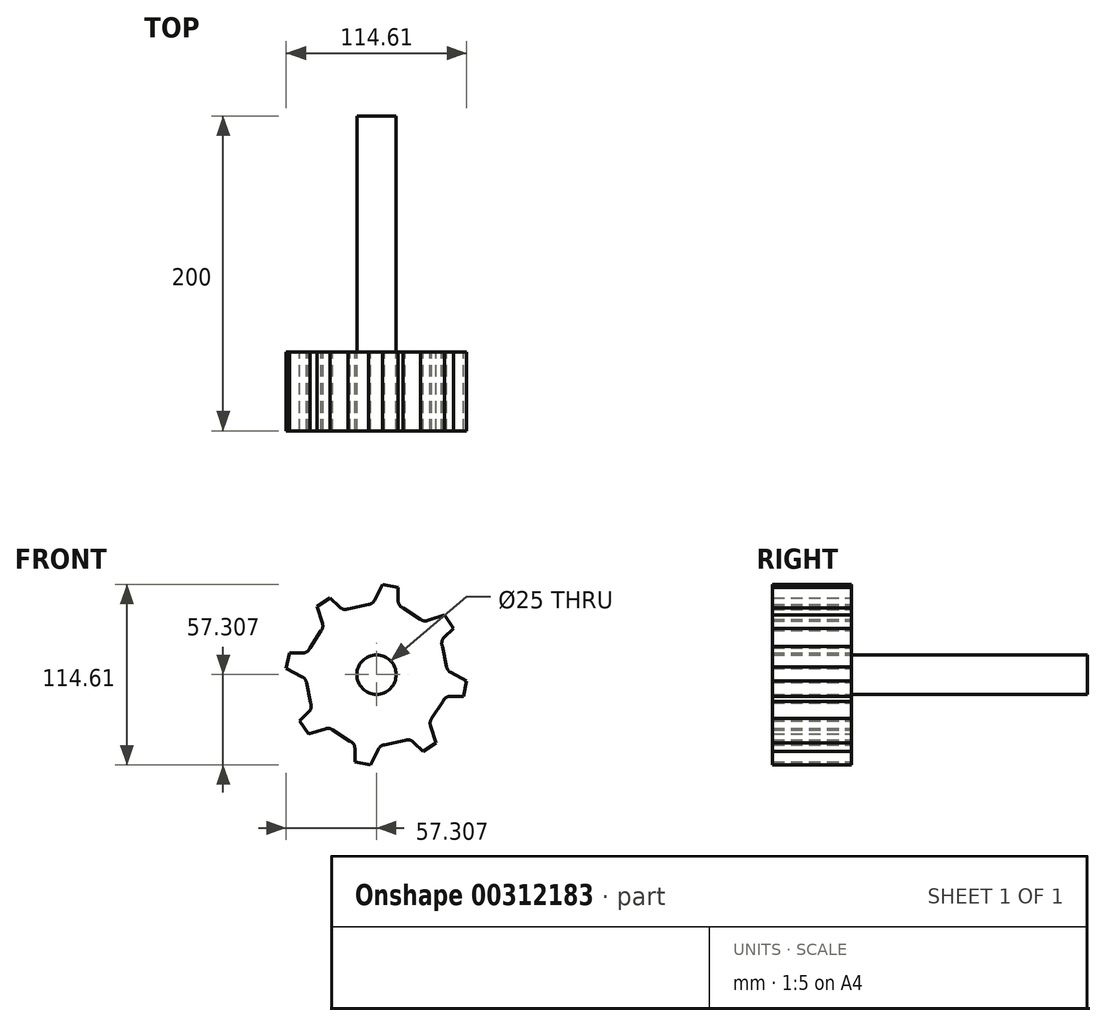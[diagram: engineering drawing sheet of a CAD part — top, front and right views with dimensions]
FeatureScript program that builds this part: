
annotation { "Feature Type Name" : "Feature", "Feature Type Description" : "" }
export const myFeature = defineFeature(function(context is Context, id is Id, definition is map)
    precondition{}
    {
        {
            var Q0;
            Q0=qCreatedBy(makeId("Front.planeOp"),FACE);
            var sketch = newSketch(context, id + "F0", { "sketchPlane" : qUnion([Q0])});
            skLineSegment(sketch, "E0.bottom", {"start": v(250, -250) * mm, "end": v(-250, -250) * mm});
            skLineSegment(sketch, "E0.top", {"start": v(250, 250) * mm, "end": v(-250, 250) * mm});
            skLineSegment(sketch, "E0.left", {"start": v(250, -250) * mm, "end": v(250, 250) * mm});
            skLineSegment(sketch, "E0.right", {"start": v(-250, -250) * mm, "end": v(-250, 250) * mm});
            skLineSegment(sketch, "E1", {"start": v(-125.88, -126.38) * mm, "end": v(-116.04, -128.34) * mm});
            skLineSegment(sketch, "E2", {"start": v(-116.04, -128.34) * mm, "end": v(-116.04, -136.75) * mm});
            skLineSegment(sketch, "E3", {"start": v(-125.88, -126.38) * mm, "end": v(-131.1, -136.48) * mm});
            skPoint(sketch, "E4.visualSharp", {"position": v(-116.04, -140.12) * mm});
            skArc(sketch, "E4.filletArc", {"start": v(-116.04, -136.75) * mm, "mid": v(-115.18, -139.55) * mm, "end": v(-112.9, -141.39) * mm});
            skPoint(sketch, "E5.visualSharp", {"position": v(-132.28, -138.75) * mm});
            skArc(sketch, "E5.filletArc", {"start": v(-134.8, -139.13) * mm, "mid": v(-132.63, -138.25) * mm, "end": v(-131.1, -136.48) * mm});
            skLineSegment(sketch, "E6.1.0", {"start": v(-159.2, -134.84) * mm, "end": v(-153.25, -140.78) * mm});
            skArc(sketch, "E6.1.1", {"start": v(-153.25, -140.78) * mm, "mid": v(-150.66, -142.16) * mm, "end": v(-147.76, -141.85) * mm});
            skLineSegment(sketch, "E6.1.3", {"start": v(-167.54, -140.4) * mm, "end": v(-159.2, -134.84) * mm});
            skLineSegment(sketch, "E6.1.4", {"start": v(-167.54, -140.4) * mm, "end": v(-164.09, -151.25) * mm});
            skArc(sketch, "E6.1.5", {"start": v(-164.83, -155.74) * mm, "mid": v(-163.92, -153.58) * mm, "end": v(-164.09, -151.25) * mm});
            skLineSegment(sketch, "E6.1.6", {"start": v(-164.83, -155.74) * mm, "end": v(-166.01, -157.33) * mm});
            skLineSegment(sketch, "E6.2.0", {"start": v(-185.11, -169.95) * mm, "end": v(-176.7, -169.95) * mm});
            skArc(sketch, "E6.2.1", {"start": v(-176.7, -169.95) * mm, "mid": v(-173.9, -169.1) * mm, "end": v(-172.07, -166.82) * mm});
            skLineSegment(sketch, "E6.2.3", {"start": v(-187.08, -179.8) * mm, "end": v(-185.11, -169.95) * mm});
            skLineSegment(sketch, "E6.2.4", {"start": v(-187.08, -179.8) * mm, "end": v(-176.98, -185.01) * mm});
            skArc(sketch, "E6.2.5", {"start": v(-174.33, -188.72) * mm, "mid": v(-175.2, -186.54) * mm, "end": v(-176.98, -185.01) * mm});
            skLineSegment(sketch, "E6.3.0", {"start": v(-178.62, -213.1) * mm, "end": v(-172.67, -207.16) * mm});
            skArc(sketch, "E6.3.1", {"start": v(-172.67, -207.16) * mm, "mid": v(-171.3, -204.57) * mm, "end": v(-171.6, -201.67) * mm});
            skLineSegment(sketch, "E6.3.3", {"start": v(-173.05, -221.45) * mm, "end": v(-178.62, -213.1) * mm});
            skLineSegment(sketch, "E6.3.4", {"start": v(-173.05, -221.45) * mm, "end": v(-162.21, -218) * mm});
            skArc(sketch, "E6.3.5", {"start": v(-157.72, -218.74) * mm, "mid": v(-159.87, -217.83) * mm, "end": v(-162.21, -218) * mm});
            skLineSegment(sketch, "E6.4.0", {"start": v(-143.5, -239.02) * mm, "end": v(-143.5, -230.62) * mm});
            skArc(sketch, "E6.4.1", {"start": v(-143.5, -230.62) * mm, "mid": v(-144.36, -227.82) * mm, "end": v(-146.64, -225.98) * mm});
            skLineSegment(sketch, "E6.4.3", {"start": v(-133.67, -241) * mm, "end": v(-143.5, -239.02) * mm});
            skLineSegment(sketch, "E6.4.4", {"start": v(-133.67, -241) * mm, "end": v(-128.44, -230.89) * mm});
            skArc(sketch, "E6.4.5", {"start": v(-124.74, -228.24) * mm, "mid": v(-126.91, -229.11) * mm, "end": v(-128.44, -230.89) * mm});
            skLineSegment(sketch, "E6.5.0", {"start": v(-100.36, -232.53) * mm, "end": v(-106.3, -226.58) * mm});
            skArc(sketch, "E6.5.1", {"start": v(-106.3, -226.58) * mm, "mid": v(-108.88, -225.2) * mm, "end": v(-111.79, -225.52) * mm});
            skLineSegment(sketch, "E6.5.3", {"start": v(-92, -226.96) * mm, "end": v(-100.36, -232.53) * mm});
            skLineSegment(sketch, "E6.5.4", {"start": v(-92, -226.96) * mm, "end": v(-95.46, -216.12) * mm});
            skArc(sketch, "E6.5.5", {"start": v(-94.71, -211.63) * mm, "mid": v(-95.62, -213.78) * mm, "end": v(-95.46, -216.12) * mm});
            skLineSegment(sketch, "E6.6.0", {"start": v(-74.43, -197.42) * mm, "end": v(-82.84, -197.42) * mm});
            skArc(sketch, "E6.6.1", {"start": v(-82.84, -197.42) * mm, "mid": v(-85.64, -198.27) * mm, "end": v(-87.48, -200.55) * mm});
            skLineSegment(sketch, "E6.6.3", {"start": v(-72.47, -187.58) * mm, "end": v(-74.43, -197.42) * mm});
            skLineSegment(sketch, "E6.6.4", {"start": v(-72.47, -187.58) * mm, "end": v(-82.57, -182.35) * mm});
            skArc(sketch, "E6.6.5", {"start": v(-85.22, -178.65) * mm, "mid": v(-84.34, -180.82) * mm, "end": v(-82.57, -182.35) * mm});
            skLineSegment(sketch, "E6.7.0", {"start": v(-80.93, -154.27) * mm, "end": v(-86.87, -160.2) * mm});
            skArc(sketch, "E6.7.1", {"start": v(-86.87, -160.2) * mm, "mid": v(-88.25, -162.8) * mm, "end": v(-87.94, -165.7) * mm});
            skLineSegment(sketch, "E6.7.3", {"start": v(-86.5, -145.91) * mm, "end": v(-80.93, -154.27) * mm});
            skLineSegment(sketch, "E6.7.4", {"start": v(-86.5, -145.91) * mm, "end": v(-97.34, -149.37) * mm});
            skArc(sketch, "E6.7.5", {"start": v(-101.83, -148.62) * mm, "mid": v(-99.67, -149.53) * mm, "end": v(-97.34, -149.37) * mm});
            skPoint(sketch, "E6.center", {"position": v(-129.77, -183.68) * mm});
            skLineSegment(sketch, "E7", {"start": v(-172.07, -166.82) * mm, "end": v(-164.83, -155.74) * mm});
            skLineSegment(sketch, "E8", {"start": v(-147.76, -141.85) * mm, "end": v(-134.8, -139.13) * mm});
            skLineSegment(sketch, "E9", {"start": v(-112.9, -141.39) * mm, "end": v(-101.83, -148.62) * mm});
            skLineSegment(sketch, "E10", {"start": v(-87.94, -165.7) * mm, "end": v(-85.22, -178.65) * mm});
            skLineSegment(sketch, "E11", {"start": v(-94.71, -211.63) * mm, "end": v(-87.48, -200.55) * mm});
            skLineSegment(sketch, "E12", {"start": v(-124.74, -228.24) * mm, "end": v(-111.79, -225.52) * mm});
            skLineSegment(sketch, "E13", {"start": v(-157.72, -218.74) * mm, "end": v(-146.64, -225.98) * mm});
            skLineSegment(sketch, "E14", {"start": v(-174.33, -188.72) * mm, "end": v(-171.6, -201.67) * mm});
            skCircle(sketch, "E15", {"center": v(-129.77, -183.68) * mm, "radius": 12.5 * mm});
            skSolve(sketch);
        }
        {
            var Q0;
            Q0=makeQuery(id+"F0.imprint","IMPRINT",FACE,{"disambiguationData":[TD([[makeQuery(id+"F0.imprint","IMPRINT",EDGE,{"derivedFrom":sQuery(id+"F0.wireOp",EDGE,"E1")}),-1.0]])]});
            extrude(context, id + "F1", {"entities" : qUnion([Q0]), "depth" : 50 * mm});
        }
        {
            var Q0;
            Q0=makeQuery(id+"F1.opExtrude","CAP_FACE",FACE,{"disambiguationData":[OSD([sQuery(id+"F0.wireOp",EDGE,"E1"),sQuery(id+"F0.wireOp",EDGE,"E2"),sQuery(id+"F0.wireOp",EDGE,"E3"),sQuery(id+"F0.wireOp",EDGE,"E4.filletArc"),sQuery(id+"F0.wireOp",EDGE,"E5.filletArc"),sQuery(id+"F0.wireOp",EDGE,"E6.1.0"),sQuery(id+"F0.wireOp",EDGE,"E6.1.1"),sQuery(id+"F0.wireOp",EDGE,"E6.1.3"),sQuery(id+"F0.wireOp",EDGE,"E6.1.4"),sQuery(id+"F0.wireOp",EDGE,"E6.1.5"),sQuery(id+"F0.wireOp",EDGE,"E6.2.0"),sQuery(id+"F0.wireOp",EDGE,"E6.2.1"),sQuery(id+"F0.wireOp",EDGE,"E6.2.3"),sQuery(id+"F0.wireOp",EDGE,"E6.2.4"),sQuery(id+"F0.wireOp",EDGE,"E6.2.5"),sQuery(id+"F0.wireOp",EDGE,"E6.3.0"),sQuery(id+"F0.wireOp",EDGE,"E6.3.1"),sQuery(id+"F0.wireOp",EDGE,"E6.3.3"),sQuery(id+"F0.wireOp",EDGE,"E6.3.4"),sQuery(id+"F0.wireOp",EDGE,"E6.3.5"),sQuery(id+"F0.wireOp",EDGE,"E6.4.0"),sQuery(id+"F0.wireOp",EDGE,"E6.4.1"),sQuery(id+"F0.wireOp",EDGE,"E6.4.3"),sQuery(id+"F0.wireOp",EDGE,"E6.4.4"),sQuery(id+"F0.wireOp",EDGE,"E6.4.5"),sQuery(id+"F0.wireOp",EDGE,"E6.5.0"),sQuery(id+"F0.wireOp",EDGE,"E6.5.1"),sQuery(id+"F0.wireOp",EDGE,"E6.5.3"),sQuery(id+"F0.wireOp",EDGE,"E6.5.4"),sQuery(id+"F0.wireOp",EDGE,"E6.5.5"),sQuery(id+"F0.wireOp",EDGE,"E6.6.0"),sQuery(id+"F0.wireOp",EDGE,"E6.6.1"),sQuery(id+"F0.wireOp",EDGE,"E6.6.3"),sQuery(id+"F0.wireOp",EDGE,"E6.6.4"),sQuery(id+"F0.wireOp",EDGE,"E6.6.5"),sQuery(id+"F0.wireOp",EDGE,"E6.7.0"),sQuery(id+"F0.wireOp",EDGE,"E6.7.1"),sQuery(id+"F0.wireOp",EDGE,"E6.7.3"),sQuery(id+"F0.wireOp",EDGE,"E6.7.4"),sQuery(id+"F0.wireOp",EDGE,"E6.7.5"),sQuery(id+"F0.wireOp",EDGE,"E7"),sQuery(id+"F0.wireOp",EDGE,"E8"),sQuery(id+"F0.wireOp",EDGE,"E9"),sQuery(id+"F0.wireOp",EDGE,"E10"),sQuery(id+"F0.wireOp",EDGE,"E11"),sQuery(id+"F0.wireOp",EDGE,"E12"),sQuery(id+"F0.wireOp",EDGE,"E13"),sQuery(id+"F0.wireOp",EDGE,"E14"),sQuery(id+"F0.wireOp",EDGE,"E15")])],"isStart":true});
            var sketch = newSketch(context, id + "F2", { "sketchPlane" : qUnion([Q0])});
            skCircle(sketch, "E16.0", {"center": v(129.77, -183.68) * mm, "radius": 12.5 * mm});
            skSolve(sketch);
        }
        {
            var Q0;
            Q0=makeQuery(id+"F2.imprint","IMPRINT",FACE,{"disambiguationData":[TD([[makeQuery(id+"F2.imprint","IMPRINT",EDGE,{"derivedFrom":sQuery(id+"F2.wireOp",EDGE,"E16.0")}),-1.0]])]});
            extrude(context, id + "F3", {"entities" : qUnion([Q0]), "depth" : 150 * mm});
        }
    });
